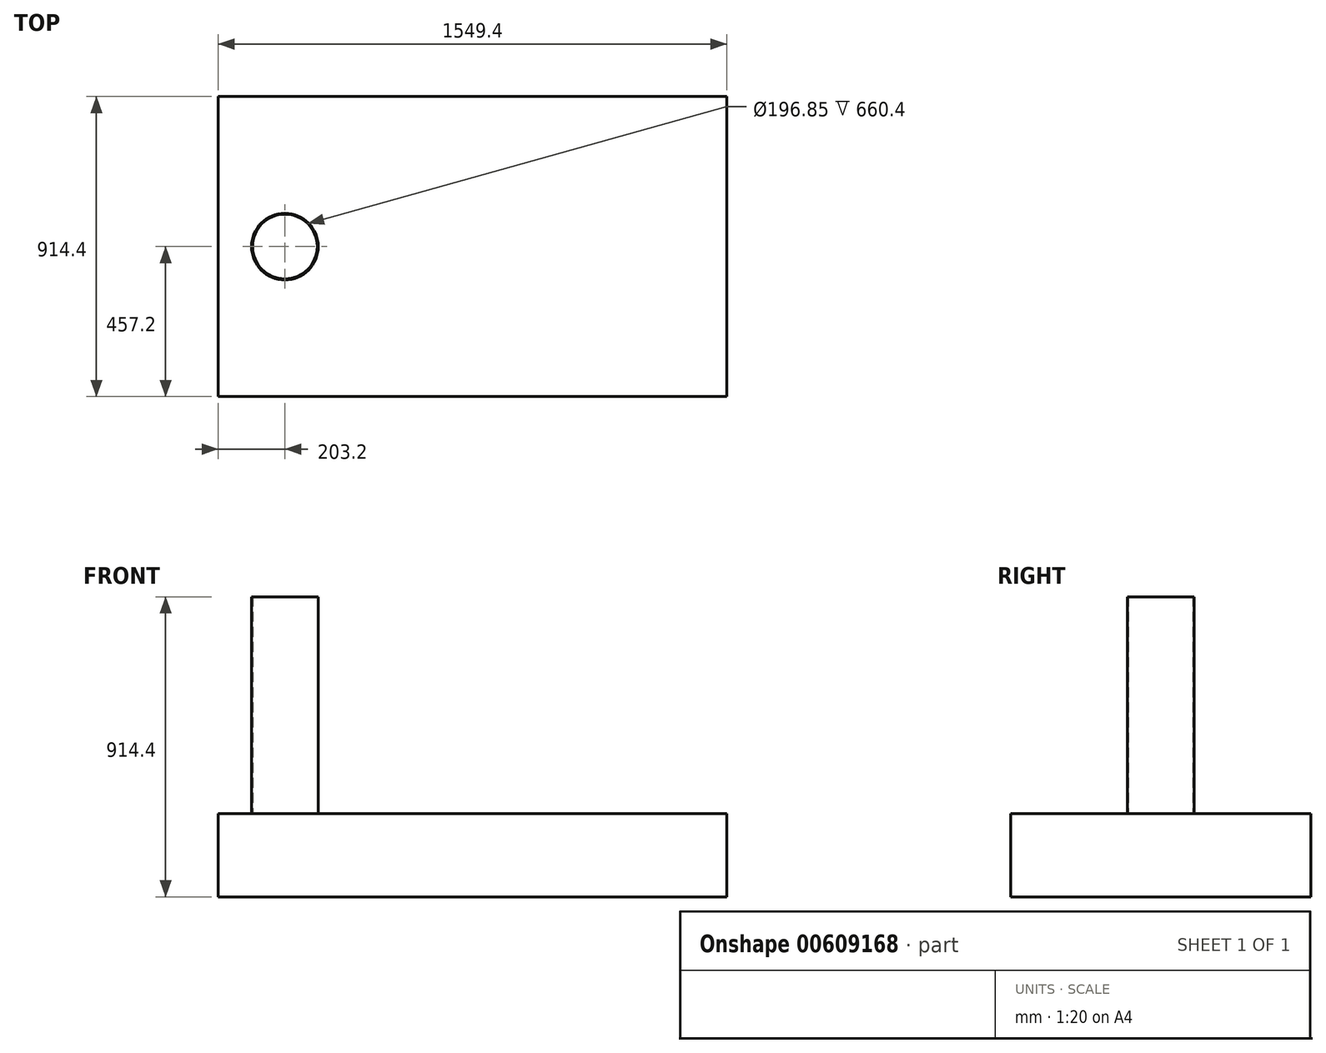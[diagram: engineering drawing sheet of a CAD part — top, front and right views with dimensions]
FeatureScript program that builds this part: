
annotation { "Feature Type Name" : "Feature", "Feature Type Description" : "" }
export const myFeature = defineFeature(function(context is Context, id is Id, definition is map)
    precondition{}
    {
        {
            var Q0;
            Q0=qCreatedBy(makeId("Top.planeOp"),FACE);
            var sketch = newSketch(context, id + "F0", { "sketchPlane" : qUnion([Q0])});
            skLineSegment(sketch, "E0.bottom", {"start": v(774.7, 457.2) * mm, "end": v(-774.7, 457.2) * mm});
            skLineSegment(sketch, "E0.top", {"start": v(774.7, -457.2) * mm, "end": v(-774.7, -457.2) * mm});
            skLineSegment(sketch, "E0.left", {"start": v(774.7, 457.2) * mm, "end": v(774.7, -457.2) * mm});
            skLineSegment(sketch, "E0.right", {"start": v(-774.7, 457.2) * mm, "end": v(-774.7, -457.2) * mm});
            skPoint(sketch, "E0.middle", {"position": v(0, 0) * mm});
            skSolve(sketch);
        }
        {
            var Q0;
            Q0=makeQuery(id+"F0.imprint","IMPRINT",FACE,{"disambiguationData":[TD([[makeQuery(id+"F0.imprint","IMPRINT",EDGE,{"derivedFrom":sQuery(id+"F0.wireOp",EDGE,"E0.bottom")}),1.0]])]});
            extrude(context, id + "F1", {"entities" : qUnion([Q0]), "depth" : 254 * mm, "offsetDistance" : 25.4 * mm});
        }
        {
            var Q0;
            Q0=makeQuery(id+"F1.opExtrude","CAP_FACE",FACE,{"disambiguationData":[OSD([sQuery(id+"F0.wireOp",EDGE,"E0.bottom"),sQuery(id+"F0.wireOp",EDGE,"E0.top"),sQuery(id+"F0.wireOp",EDGE,"E0.left"),sQuery(id+"F0.wireOp",EDGE,"E0.right")])],"isStart":false});
            var sketch = newSketch(context, id + "F2", { "sketchPlane" : qUnion([Q0])});
            skCircle(sketch, "E1", {"center": v(-571.5, 0) * mm, "radius": 101.6 * mm});
            skLineSegment(sketch, "E2", {"start": v(-571.5, 0) * mm, "end": v(0, 0) * mm, "construction": true});
            skCircle(sketch, "E3", {"center": v(-571.5, 0) * mm, "radius": 98.43 * mm});
            skSolve(sketch);
        }
        {
            var Q0;
            Q0 = qSketchRegion(id + "F2", true);
            extrude(context, id + "F3", {"entities" : qUnion([Q0]), "operationType" : NewBodyOperationType.ADD, "depth" : 660.4 * mm, "offsetDistance" : 25.4 * mm});
        }
    });
